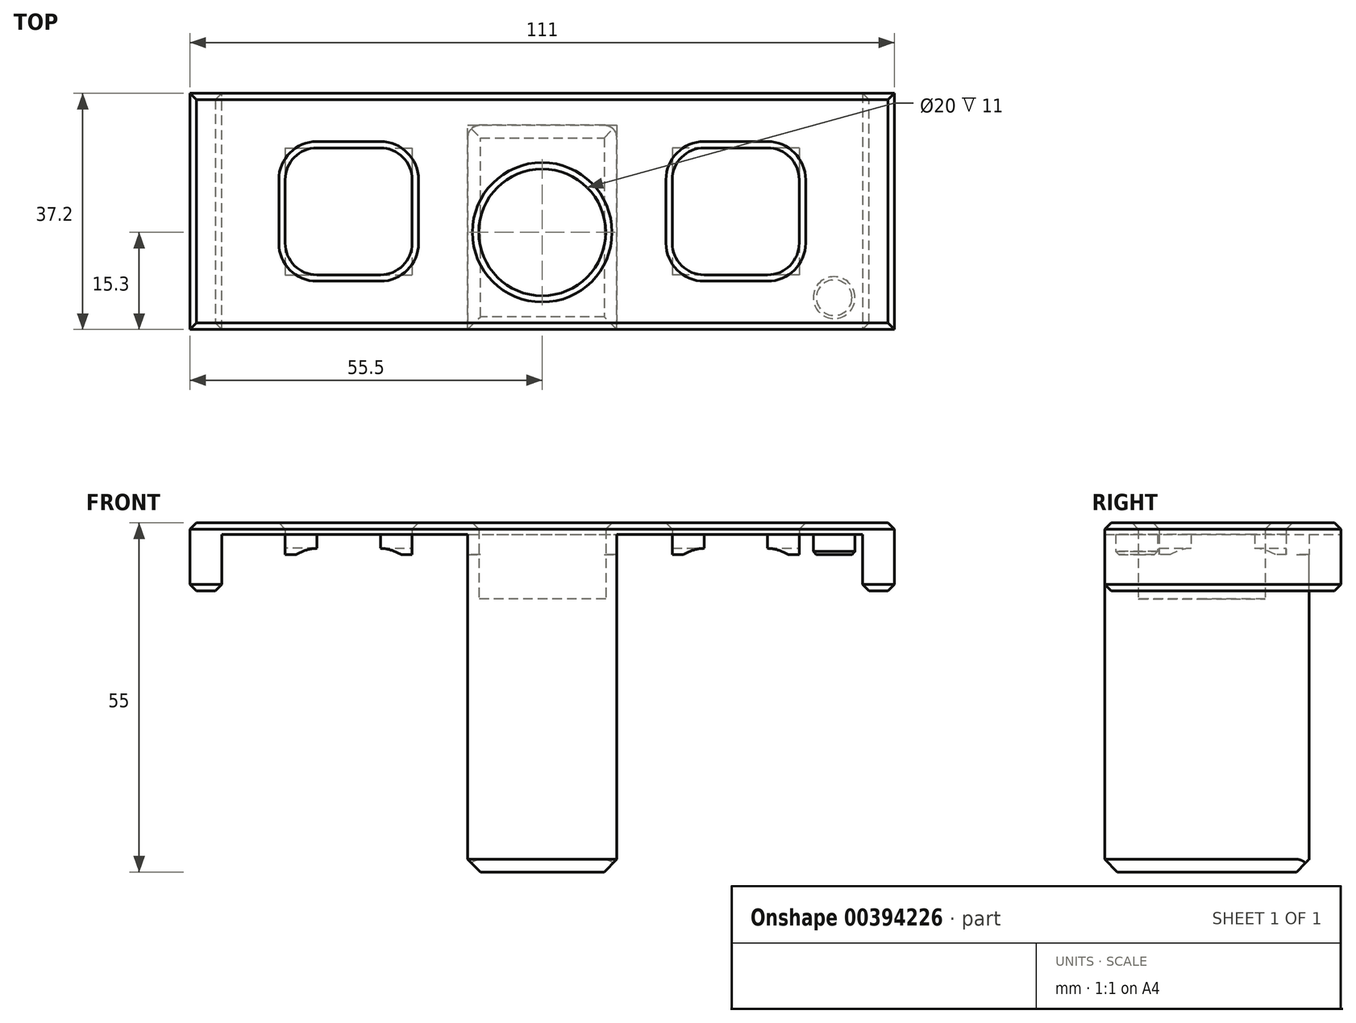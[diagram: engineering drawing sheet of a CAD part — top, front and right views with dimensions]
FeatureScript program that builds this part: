
annotation { "Feature Type Name" : "Feature", "Feature Type Description" : "" }
export const myFeature = defineFeature(function(context is Context, id is Id, definition is map)
    precondition{}
    {
        {
            var Q0;
            Q0=qCreatedBy(makeId("Top.planeOp"),FACE);
            var sketch = newSketch(context, id + "F0", { "sketchPlane" : qUnion([Q0])});
            skLineSegment(sketch, "E0", {"start": v(60, 0) * mm, "end": v(-60, 0) * mm, "construction": true});
            skPoint(sketch, "E1", {"position": v(0, 0) * mm});
            skLineSegment(sketch, "E2", {"start": v(60, 0) * mm, "end": v(60, 49.4) * mm, "construction": true});
            skLineSegment(sketch, "E3", {"start": v(-60, 0) * mm, "end": v(-60, 49.4) * mm, "construction": true});
            skArc(sketch, "E4", {"start": v(-60, 49.4) * mm, "mid": v(0, 109.4) * mm, "end": v(60, 49.4) * mm, "construction": true});
            skLineSegment(sketch, "E5.bottom", {"start": v(-9.5, 35.6) * mm, "end": v(9.5, 35.6) * mm, "construction": true});
            skLineSegment(sketch, "E5.top", {"start": v(-9.5, 16.6) * mm, "end": v(9.5, 16.6) * mm, "construction": true});
            skLineSegment(sketch, "E5.left", {"start": v(-9.5, 35.6) * mm, "end": v(-9.5, 16.6) * mm, "construction": true});
            skLineSegment(sketch, "E5.right", {"start": v(9.5, 35.6) * mm, "end": v(9.5, 16.6) * mm, "construction": true});
            skPoint(sketch, "E5.middle", {"position": v(0, 26.1) * mm});
            skLineSegment(sketch, "E6.top", {"start": v(-11.75, 43) * mm, "end": v(11.75, 43) * mm, "construction": true});
            skLineSegment(sketch, "E6.left", {"start": v(-11.75, 0) * mm, "end": v(-11.75, 43) * mm, "construction": true});
            skLineSegment(sketch, "E6.right", {"start": v(11.75, 0) * mm, "end": v(11.75, 43) * mm, "construction": true});
            skPoint(sketch, "E7", {"position": v(0, 43) * mm});
            skCircle(sketch, "E8", {"center": v(0, 61) * mm, "radius": 2.5 * mm});
            skCircle(sketch, "E9", {"center": v(0, 26.1) * mm, "radius": 10 * mm});
            skLineSegment(sketch, "E10", {"start": v(-50.5, 0) * mm, "end": v(-50.5, 49.4) * mm, "construction": true});
            skLineSegment(sketch, "E11", {"start": v(50.5, 0) * mm, "end": v(50.5, 49.4) * mm, "construction": true});
            skArc(sketch, "E12", {"start": v(50.5, 49.4) * mm, "mid": v(0, 99.9) * mm, "end": v(-50.5, 49.4) * mm, "construction": true});
            skLineSegment(sketch, "E13", {"start": v(-55.5, 10.8) * mm, "end": v(55.5, 10.8) * mm});
            skLineSegment(sketch, "E14", {"start": v(-5, 48) * mm, "end": v(-55.5, 48) * mm});
            skLineSegment(sketch, "E15", {"start": v(-55.5, 48) * mm, "end": v(-55.5, 10.8) * mm});
            skLineSegment(sketch, "E16", {"start": v(5, 48) * mm, "end": v(55.5, 48) * mm});
            skLineSegment(sketch, "E17", {"start": v(55.5, 48) * mm, "end": v(55.5, 10.8) * mm});
            skLineSegment(sketch, "E18", {"start": v(-11.75, 10.8) * mm, "end": v(-11.75, 43) * mm});
            skLineSegment(sketch, "E19", {"start": v(11.75, 43) * mm, "end": v(11.75, 10.8) * mm});
            skLineSegment(sketch, "E20", {"start": v(-11.75, 43) * mm, "end": v(11.75, 43) * mm});
            skLineSegment(sketch, "E21", {"start": v(-50.5, 10.8) * mm, "end": v(-50.5, 48) * mm});
            skLineSegment(sketch, "E22", {"start": v(50.5, 10.8) * mm, "end": v(50.5, 48) * mm});
            skLineSegment(sketch, "E23.bottom", {"start": v(-40.5, 39.4) * mm, "end": v(-20.5, 39.4) * mm});
            skLineSegment(sketch, "E23.top", {"start": v(-40.5, 19.4) * mm, "end": v(-20.5, 19.4) * mm});
            skLineSegment(sketch, "E23.left", {"start": v(-40.5, 39.4) * mm, "end": v(-40.5, 19.4) * mm});
            skLineSegment(sketch, "E23.right", {"start": v(-20.5, 39.4) * mm, "end": v(-20.5, 19.4) * mm});
            skPoint(sketch, "E23.middle", {"position": v(-30.5, 29.4) * mm});
            skPoint(sketch, "E24", {"position": v(-50.5, 29.4) * mm});
            skLineSegment(sketch, "E25.MirrorCS", {"start": v(40.5, 39.4) * mm, "end": v(20.5, 39.4) * mm});
            skLineSegment(sketch, "E26.MirrorCS", {"start": v(20.5, 39.4) * mm, "end": v(20.5, 19.4) * mm});
            skLineSegment(sketch, "E27.MirrorCS", {"start": v(40.5, 19.4) * mm, "end": v(20.5, 19.4) * mm});
            skLineSegment(sketch, "E28.MirrorCS", {"start": v(40.5, 39.4) * mm, "end": v(40.5, 19.4) * mm});
            skLineSegment(sketch, "E29", {"start": v(-5, 48) * mm, "end": v(5, 48) * mm});
            skSolve(sketch);
        }
        {
            var Q0;
            {var subQ0=sQuery(id+"F0.wireOp",EDGE,"E17");Q0=makeQuery(id+"F0.imprint","IMPRINT",FACE,{"disambiguationData":[TD([[makeQuery(id+"F0.imprint","IMPRINT",EDGE,{"derivedFrom":subQ0}),-1.0]])]});}
            var Q1;
            Q1=makeQuery(id+"F0.imprint","IMPRINT",FACE,{"disambiguationData":[TD([[makeQuery(id+"F0.imprint","IMPRINT",EDGE,{"derivedFrom":sQuery(id+"F0.wireOp",EDGE,"E8")}),-1.0]])]});
            var Q2;
            {var subQ0=sQuery(id+"F0.wireOp",EDGE,"E15");Q2=makeQuery(id+"F0.imprint","IMPRINT",FACE,{"disambiguationData":[TD([[makeQuery(id+"F0.imprint","IMPRINT",EDGE,{"derivedFrom":subQ0}),1.0]])]});}
            var Q3;
            Q3=makeQuery(id+"F0.imprint","IMPRINT",FACE,{"disambiguationData":[TD([[makeQuery(id+"F0.imprint","IMPRINT",EDGE,{"derivedFrom":sQuery(id+"F0.wireOp",EDGE,"E9")}),-1.0]])]});
            var Q4;
            {var subQ1=sQuery(id+"F0.wireOp",EDGE,"E18");Q4=makeQuery(id+"F0.imprint","IMPRINT",FACE,{"disambiguationData":[TD([[makeQuery(id+"F0.imprint","IMPRINT",EDGE,{"derivedFrom":subQ1}),1.0]])]});}
            extrude(context, id + "F1", {"entities" : qUnion([Q0, Q1, Q2, Q3, Q4]), "depth" : 5 * mm});
        }
        {
            var Q0;
            {var subQ0=sQuery(id+"F0.wireOp",EDGE,"E15");Q0=makeQuery(id+"F0.imprint","IMPRINT",FACE,{"disambiguationData":[TD([[makeQuery(id+"F0.imprint","IMPRINT",EDGE,{"derivedFrom":subQ0}),1.0]])]});}
            var Q1;
            {var subQ0=sQuery(id+"F0.wireOp",EDGE,"E17");Q1=makeQuery(id+"F0.imprint","IMPRINT",FACE,{"disambiguationData":[TD([[makeQuery(id+"F0.imprint","IMPRINT",EDGE,{"derivedFrom":subQ0}),-1.0]])]});}
            extrude(context, id + "F2", {"entities" : qUnion([Q0, Q1]), "operationType" : NewBodyOperationType.ADD, "oppositeDirection" : true, "depth" : 5.7 * mm});
        }
        {
            var Q0;
            Q0=makeQuery(id+"F0.imprint","IMPRINT",FACE,{"disambiguationData":[TD([[makeQuery(id+"F0.imprint","IMPRINT",EDGE,{"derivedFrom":sQuery(id+"F0.wireOp",EDGE,"E9")}),-1.0]])]});
            extrude(context, id + "F3", {"entities" : qUnion([Q0]), "operationType" : NewBodyOperationType.ADD, "oppositeDirection" : true, "depth" : 7 * mm});
        }
        {
            var Q0;
            Q0=makeQuery(id+"F3.opExtrude","CAP_FACE",FACE,{"disambiguationData":[OSD([sQuery(id+"F0.wireOp",EDGE,"E9"),sQuery(id+"F0.wireOp",EDGE,"E13"),sQuery(id+"F0.wireOp",EDGE,"E18"),sQuery(id+"F0.wireOp",EDGE,"E19"),sQuery(id+"F0.wireOp",EDGE,"E20")])],"isStart":false});
            var sketch = newSketch(context, id + "F4", { "sketchPlane" : qUnion([Q0])});
            skCircle(sketch, "E30.0", {"center": v(0, -26.1) * mm, "radius": 10 * mm});
            skLineSegment(sketch, "E31.0", {"start": v(-11.75, -10.8) * mm, "end": v(-11.75, -43) * mm});
            skLineSegment(sketch, "E32.0", {"start": v(11.75, -43) * mm, "end": v(11.75, -10.8) * mm});
            skLineSegment(sketch, "E33.0", {"start": v(-11.75, -43) * mm, "end": v(11.75, -43) * mm});
            skLineSegment(sketch, "E34.0", {"start": v(-55.5, -10.8) * mm, "end": v(55.5, -10.8) * mm});
            skSolve(sketch);
        }
        {
            var Q0;
            Q0=makeQuery(id+"F4.imprint","IMPRINT",FACE,{"disambiguationData":[TD([[makeQuery(id+"F4.imprint","IMPRINT",EDGE,{"derivedFrom":sQuery(id+"F4.wireOp",EDGE,"E30.0")}),1.0]])]});
            var Q1;
            Q1=makeQuery(id+"F4.imprint","IMPRINT",FACE,{"disambiguationData":[TD([[makeQuery(id+"F4.imprint","IMPRINT",EDGE,{"derivedFrom":sQuery(id+"F4.wireOp",EDGE,"E30.0")}),-1.0]])]});
            extrude(context, id + "F5", {"entities" : qUnion([Q0, Q1]), "operationType" : NewBodyOperationType.ADD, "depth" : 43 * mm});
        }
        {
            var Q0;
            Q0=makeQuery(id+"F1.opExtrude","SWEPT_EDGE",EDGE,{"disambiguationData":[OSD([sQuery(id+"F0.wireOp",EDGE,"E25.MirrorCS"),sQuery(id+"F0.wireOp",EDGE,"E26.MirrorCS")])]});
            var Q1;
            Q1=makeQuery(id+"F1.opExtrude","SWEPT_EDGE",EDGE,{"disambiguationData":[OSD([sQuery(id+"F0.wireOp",EDGE,"E25.MirrorCS"),sQuery(id+"F0.wireOp",EDGE,"E28.MirrorCS")])]});
            var Q2;
            Q2=makeQuery(id+"F1.opExtrude","SWEPT_EDGE",EDGE,{"disambiguationData":[OSD([sQuery(id+"F0.wireOp",EDGE,"E26.MirrorCS"),sQuery(id+"F0.wireOp",EDGE,"E27.MirrorCS")])]});
            var Q3;
            Q3=makeQuery(id+"F1.opExtrude","SWEPT_EDGE",EDGE,{"disambiguationData":[OSD([sQuery(id+"F0.wireOp",EDGE,"E27.MirrorCS"),sQuery(id+"F0.wireOp",EDGE,"E28.MirrorCS")])]});
            var Q4;
            Q4=makeQuery(id+"F1.opExtrude","SWEPT_EDGE",EDGE,{"disambiguationData":[OSD([sQuery(id+"F0.wireOp",EDGE,"E23.bottom"),sQuery(id+"F0.wireOp",EDGE,"E23.right")])]});
            var Q5;
            Q5=makeQuery(id+"F1.opExtrude","SWEPT_EDGE",EDGE,{"disambiguationData":[OSD([sQuery(id+"F0.wireOp",EDGE,"E23.bottom"),sQuery(id+"F0.wireOp",EDGE,"E23.left")])]});
            var Q6;
            Q6=makeQuery(id+"F1.opExtrude","SWEPT_EDGE",EDGE,{"disambiguationData":[OSD([sQuery(id+"F0.wireOp",EDGE,"E23.top"),sQuery(id+"F0.wireOp",EDGE,"E23.left")])]});
            var Q7;
            Q7=makeQuery(id+"F1.opExtrude","SWEPT_EDGE",EDGE,{"disambiguationData":[OSD([sQuery(id+"F0.wireOp",EDGE,"E23.top"),sQuery(id+"F0.wireOp",EDGE,"E23.right")])]});
            fillet(context, id + "F6", {"entities" : qUnion([Q0, Q1, Q2, Q3, Q4, Q5, Q6, Q7]), "radius" : 5 * mm, "tangentPropagation" : true, "allowEdgeOverflow" : false});
        }
        {
            var Q0;
            Q0=makeQuery(id+"F5.opExtrude","CAP_FACE",FACE,{"disambiguationData":[OSD([sQuery(id+"F4.wireOp",EDGE,"E31.0"),sQuery(id+"F4.wireOp",EDGE,"E32.0"),sQuery(id+"F4.wireOp",EDGE,"E33.0"),sQuery(id+"F4.wireOp",EDGE,"E34.0")])],"isStart":false});
            chamfer(context, id + "F7", {"entities" : qUnion([Q0]), "width" : 2 * mm, "tangentPropagation" : true});
        }
        {
            var Q0;
            Q0=makeQuery(id+"F2.opExtrude","CAP_FACE",FACE,{"disambiguationData":[OSD([sQuery(id+"F0.wireOp",EDGE,"E13"),sQuery(id+"F0.wireOp",EDGE,"E16"),sQuery(id+"F0.wireOp",EDGE,"E17"),sQuery(id+"F0.wireOp",EDGE,"E22")])],"isStart":false});
            var Q1;
            Q1=makeQuery(id+"F2.opExtrude","CAP_FACE",FACE,{"disambiguationData":[OSD([sQuery(id+"F0.wireOp",EDGE,"E13"),sQuery(id+"F0.wireOp",EDGE,"E14"),sQuery(id+"F0.wireOp",EDGE,"E15"),sQuery(id+"F0.wireOp",EDGE,"E21")])],"isStart":false});
            chamfer(context, id + "F8", {"entities" : qUnion([Q0, Q1]), "width" : 1 * mm, "tangentPropagation" : true});
        }
        {
            var Q0;
            Q0=makeQuery(id+"F1.opExtrude","CAP_EDGE",EDGE,{"disambiguationData":[OSD([sQuery(id+"F0.wireOp",EDGE,"E9")])],"isStart":false});
            var Q1;
            Q1=makeQuery(id+"F1.opExtrude","CAP_FACE",FACE,{"disambiguationData":[OSD([sQuery(id+"F0.wireOp",EDGE,"E8"),sQuery(id+"F0.wireOp",EDGE,"E9"),sQuery(id+"F0.wireOp",EDGE,"E13"),sQuery(id+"F0.wireOp",EDGE,"uMwWZtNu-Dw81-lolb-aZyy-NJvXPs4QEp65"),sQuery(id+"F0.wireOp",EDGE,"Z9U0XRlE-dxfa-tuDr-xob2-sdNl3EHwIGiv"),sQuery(id+"F0.wireOp",EDGE,"E14"),sQuery(id+"F0.wireOp",EDGE,"E15"),sQuery(id+"F0.wireOp",EDGE,"00c8z8Gw-GomL-fDnv-EX9J-OPI5zF7WXmIM"),sQuery(id+"F0.wireOp",EDGE,"E16"),sQuery(id+"F0.wireOp",EDGE,"E17"),sQuery(id+"F0.wireOp",EDGE,"E23.bottom"),sQuery(id+"F0.wireOp",EDGE,"E23.top"),sQuery(id+"F0.wireOp",EDGE,"E23.left"),sQuery(id+"F0.wireOp",EDGE,"E23.right"),sQuery(id+"F0.wireOp",EDGE,"E25.MirrorCS"),sQuery(id+"F0.wireOp",EDGE,"E26.MirrorCS"),sQuery(id+"F0.wireOp",EDGE,"E27.MirrorCS"),sQuery(id+"F0.wireOp",EDGE,"E28.MirrorCS")])],"isStart":false});
            chamfer(context, id + "F9", {"entities" : qUnion([Q0, Q1]), "width" : 1 * mm, "tangentPropagation" : true});
        }
        {
            var Q0;
            Q0=makeQuery(id+"F1.opExtrude","CAP_EDGE",EDGE,{"disambiguationData":[OSD([sQuery(id+"F0.wireOp",EDGE,"E23.top")])],"isStart":true});
            var Q1;
            Q1=makeQuery(id+"F1.opExtrude","CAP_EDGE",EDGE,{"disambiguationData":[OSD([sQuery(id+"F0.wireOp",EDGE,"E23.right")])],"isStart":true});
            var Q2;
            Q2=makeQuery(id+"F1.opExtrude","CAP_EDGE",EDGE,{"disambiguationData":[OSD([sQuery(id+"F0.wireOp",EDGE,"E23.bottom")])],"isStart":true});
            var Q3;
            Q3=makeQuery(id+"F1.opExtrude","CAP_EDGE",EDGE,{"disambiguationData":[OSD([sQuery(id+"F0.wireOp",EDGE,"E23.left")])],"isStart":true});
            var Q4;
            Q4=makeQuery(id+"F1.opExtrude","CAP_EDGE",EDGE,{"disambiguationData":[OSD([sQuery(id+"F0.wireOp",EDGE,"E27.MirrorCS")])],"isStart":true});
            var Q5;
            Q5=makeQuery(id+"F1.opExtrude","CAP_EDGE",EDGE,{"disambiguationData":[OSD([sQuery(id+"F0.wireOp",EDGE,"E26.MirrorCS")])],"isStart":true});
            var Q6;
            Q6=makeQuery(id+"F1.opExtrude","CAP_EDGE",EDGE,{"disambiguationData":[OSD([sQuery(id+"F0.wireOp",EDGE,"E25.MirrorCS")])],"isStart":true});
            var Q7;
            Q7=makeQuery(id+"F1.opExtrude","CAP_EDGE",EDGE,{"disambiguationData":[OSD([sQuery(id+"F0.wireOp",EDGE,"E28.MirrorCS")])],"isStart":true});
            chamfer(context, id + "F10", {"entities" : qUnion([Q0, Q1, Q2, Q3, Q4, Q5, Q6, Q7]), "width" : 1 * mm, "tangentPropagation" : true});
        }
        {
            var Q0;
            Q0=makeQuery(id+"F5.boolean.opBoolean","MERGE",EDGE,{"derivedFrom":[makeQuery(id+"F3.opExtrude","SWEPT_EDGE",EDGE,{"disambiguationData":[OSD([sQuery(id+"F0.wireOp",EDGE,"E18"),sQuery(id+"F0.wireOp",EDGE,"E20")])]}),makeQuery(id+"F5.opExtrude","SWEPT_EDGE",EDGE,{"disambiguationData":[OSD([sQuery(id+"F4.wireOp",EDGE,"E31.0"),sQuery(id+"F4.wireOp",EDGE,"E33.0")])]})]});
            var Q1;
            Q1=makeQuery(id+"F5.boolean.opBoolean","MERGE",EDGE,{"derivedFrom":[makeQuery(id+"F3.opExtrude","SWEPT_EDGE",EDGE,{"disambiguationData":[OSD([sQuery(id+"F0.wireOp",EDGE,"E19"),sQuery(id+"F0.wireOp",EDGE,"E20")])]}),makeQuery(id+"F5.opExtrude","SWEPT_EDGE",EDGE,{"disambiguationData":[OSD([sQuery(id+"F4.wireOp",EDGE,"E32.0"),sQuery(id+"F4.wireOp",EDGE,"E33.0")])]})]});
            fillet(context, id + "F11", {"entities" : qUnion([Q0, Q1]), "radius" : 2 * mm, "tangentPropagation" : true, "allowEdgeOverflow" : false});
        }
        {
            var Q0;
            {var subQ1=sQuery(id+"F0.wireOp",EDGE,"E18");Q0=makeQuery(id+"F0.imprint","IMPRINT",FACE,{"disambiguationData":[TD([[makeQuery(id+"F0.imprint","IMPRINT",EDGE,{"derivedFrom":subQ1}),1.0]])]});}
            var sketch = newSketch(context, id + "F12", { "sketchPlane" : qUnion([Q0])});
            skCircle(sketch, "E35", {"center": v(-46, 43) * mm, "radius": 3.3 * mm});
            skCircle(sketch, "E36.MirrorC", {"center": v(46, 15.8) * mm, "radius": 3.3 * mm});
            skSolve(sketch);
        }
        {
            var Q0;
            Q0=makeQuery(id+"F12.imprint","IMPRINT",FACE,{"disambiguationData":[TD([[makeQuery(id+"F12.imprint","IMPRINT",EDGE,{"derivedFrom":sQuery(id+"F12.wireOp",EDGE,"E35")}),1.0]])]});
            var Q1;
            Q1=makeQuery(id+"F12.imprint","IMPRINT",FACE,{"disambiguationData":[TD([[makeQuery(id+"F12.imprint","IMPRINT",EDGE,{"derivedFrom":sQuery(id+"F12.wireOp",EDGE,"E36.MirrorC")}),-1.0]])]});
            extrude(context, id + "F13", {"entities" : qUnion([Q0, Q1]), "operationType" : NewBodyOperationType.REMOVE, "depth" : 3.2 * mm});
        }
        {
            var Q0;
            Q0=makeQuery(id+"F13.boolean.opBoolean","COPY",EDGE,{"derivedFrom":makeQuery(id+"F13.opExtrude","CAP_EDGE",EDGE,{"disambiguationData":[OSD([sQuery(id+"F12.wireOp",EDGE,"E35")])],"isStart":true})});
            var Q1;
            Q1=makeQuery(id+"F13.boolean.opBoolean","COPY",EDGE,{"derivedFrom":makeQuery(id+"F13.opExtrude","CAP_EDGE",EDGE,{"disambiguationData":[OSD([sQuery(id+"F12.wireOp",EDGE,"E36.MirrorC")])],"isStart":true})});
            chamfer(context, id + "F14", {"entities" : qUnion([Q0, Q1]), "width" : 0.5 * mm, "tangentPropagation" : true});
        }
    });
